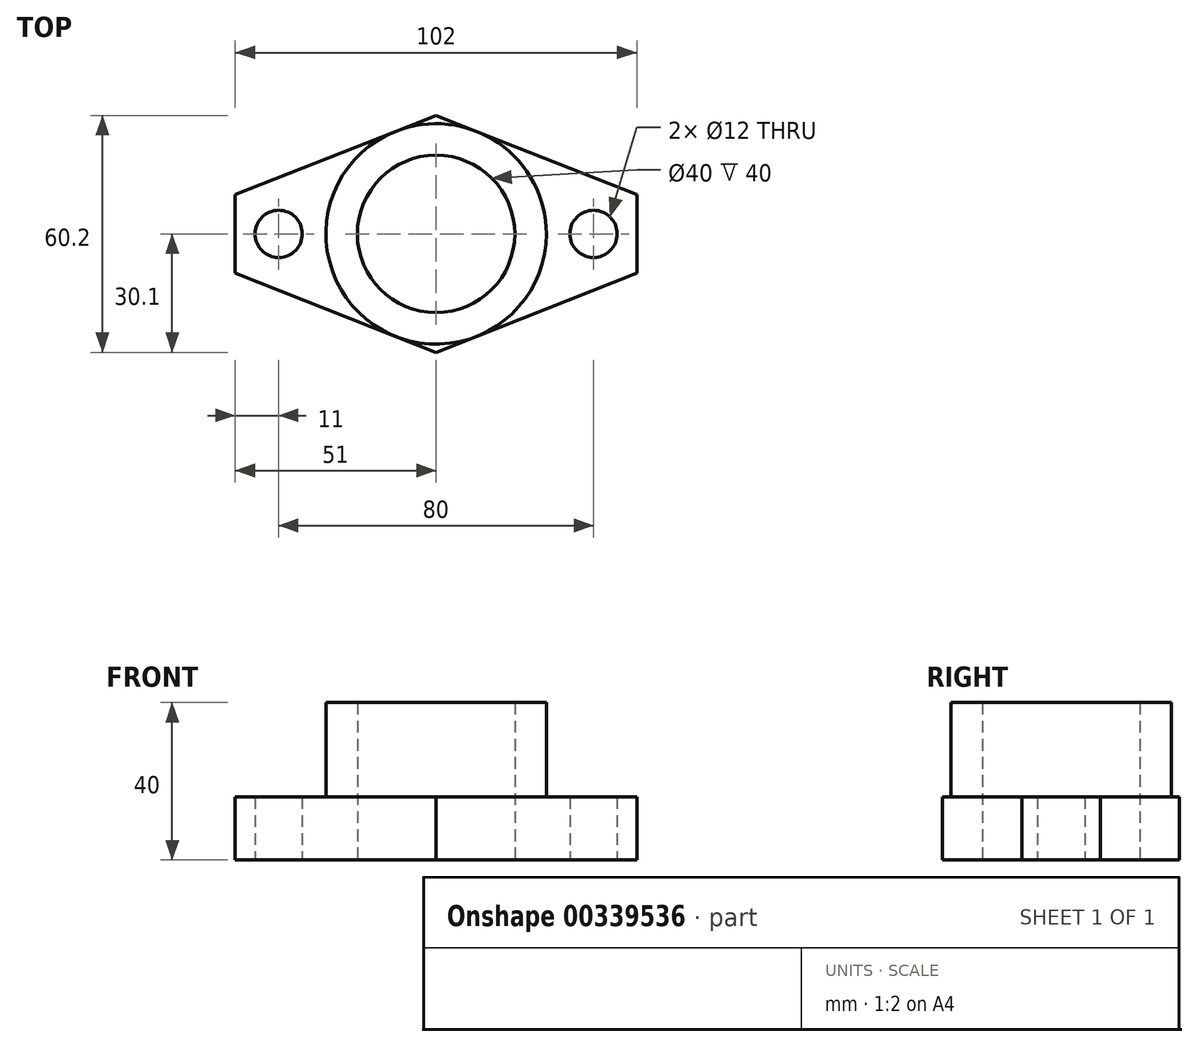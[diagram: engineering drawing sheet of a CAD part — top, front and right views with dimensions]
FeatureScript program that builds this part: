
annotation { "Feature Type Name" : "Feature", "Feature Type Description" : "" }
export const myFeature = defineFeature(function(context is Context, id is Id, definition is map)
    precondition{}
    {
        {
            var Q0;
            Q0=qCreatedBy(makeId("Top.planeOp"),FACE);
            var sketch = newSketch(context, id + "F0", { "sketchPlane" : qUnion([Q0])});
            skCircle(sketch, "E0", {"center": v(0, 0) * mm, "radius": 20 * mm});
            skCircle(sketch, "E1", {"center": v(0, 0) * mm, "radius": 28 * mm});
            skCircle(sketch, "E2", {"center": v(-40, 0) * mm, "radius": 6 * mm});
            skCircle(sketch, "E3", {"center": v(40, 0) * mm, "radius": 6 * mm});
            skLineSegment(sketch, "E4", {"start": v(-51, 10) * mm, "end": v(-51, -10) * mm});
            skLineSegment(sketch, "E5", {"start": v(51, 10) * mm, "end": v(51, -10) * mm});
            skLineSegment(sketch, "E6", {"start": v(-60.7, -10) * mm, "end": v(82.8, -10) * mm, "construction": true});
            skLineSegment(sketch, "E7", {"start": v(-51, 10) * mm, "end": v(0, 30.1) * mm});
            skLineSegment(sketch, "E8", {"start": v(0, 30.1) * mm, "end": v(51, 10) * mm});
            skLineSegment(sketch, "E9", {"start": v(-51, -10) * mm, "end": v(0, -30.1) * mm});
            skLineSegment(sketch, "E10", {"start": v(0, -30.1) * mm, "end": v(51, -10) * mm});
            skSolve(sketch);
        }
        {
            var Q0;
            Q0=makeQuery(id+"F0.imprint","IMPRINT",FACE,{"disambiguationData":[TD([[makeQuery(id+"F0.imprint","IMPRINT",EDGE,{"derivedFrom":sQuery(id+"F0.wireOp",EDGE,"E0")}),-1.0]])]});
            extrude(context, id + "F1", {"entities" : qUnion([Q0]), "flatOperationType" : FlatOperationType.REMOVE, "depth" : 40 * mm, "offsetDistance" : 25 * mm, "domain" : OperationDomain.MODEL});
        }
        {
            var Q0;
            Q0 = qSketchRegion(id + "F0", true);
            extrude(context, id + "F2", {"entities" : qUnion([Q0]), "operationType" : NewBodyOperationType.ADD, "flatOperationType" : FlatOperationType.REMOVE, "depth" : 16 * mm, "offsetDistance" : 25 * mm, "domain" : OperationDomain.MODEL});
        }
    });
